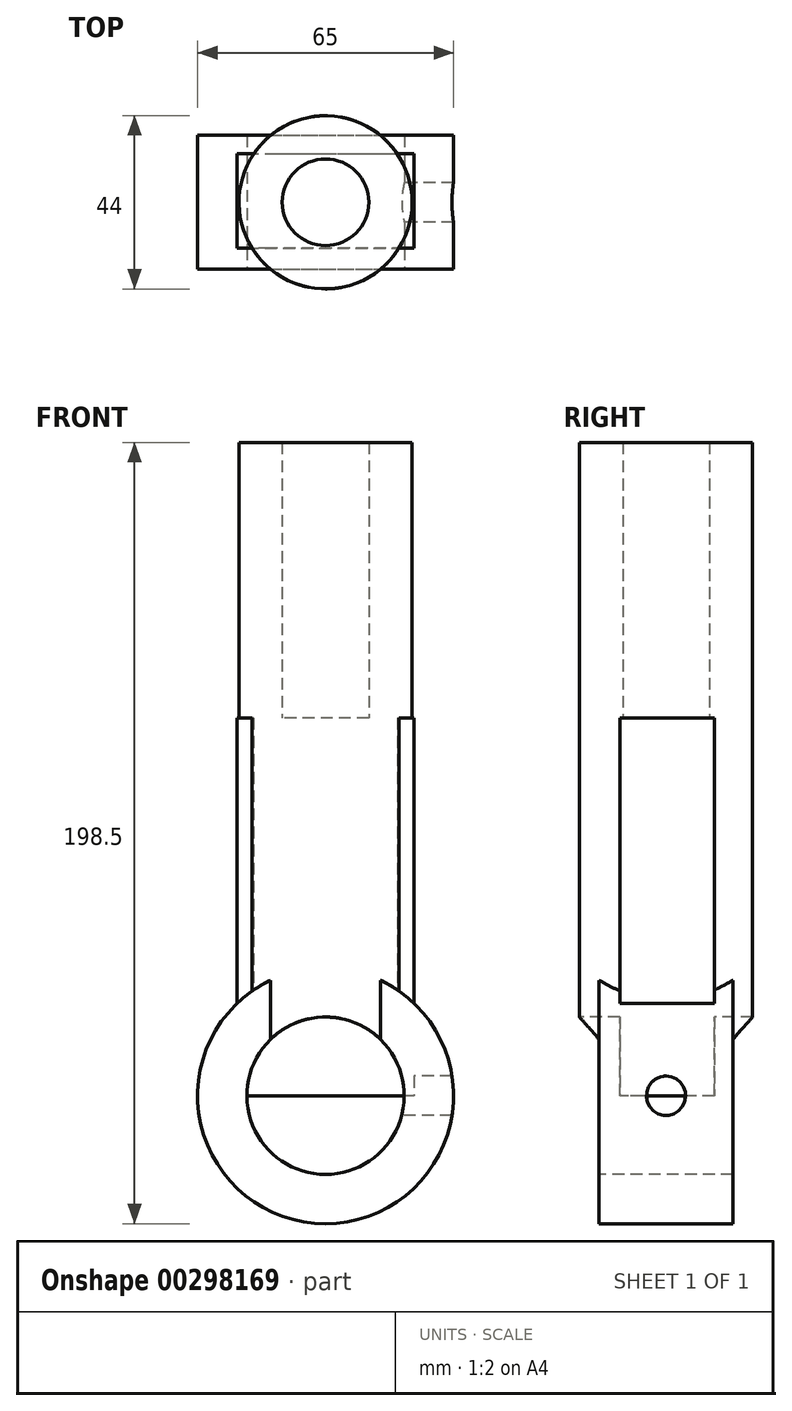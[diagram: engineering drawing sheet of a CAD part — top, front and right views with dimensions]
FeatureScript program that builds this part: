
annotation { "Feature Type Name" : "Feature", "Feature Type Description" : "" }
export const myFeature = defineFeature(function(context is Context, id is Id, definition is map)
    precondition{}
    {
        {
            var Q0;
            Q0=qCreatedBy(makeId("Front.planeOp"),FACE);
            var sketch = newSketch(context, id + "F0", { "sketchPlane" : qUnion([Q0])});
            skCircle(sketch, "E0", {"center": v(0, 0) * mm, "radius": 20 * mm});
            skCircle(sketch, "E1", {"center": v(0, 0) * mm, "radius": 32.5 * mm});
            skSolve(sketch);
        }
        {
            var Q0;
            Q0=makeQuery(id+"F0.imprint","IMPRINT",FACE,{"disambiguationData":[TD([[makeQuery(id+"F0.imprint","IMPRINT",EDGE,{"derivedFrom":sQuery(id+"F0.wireOp",EDGE,"E0")}),-1.0]])]});
            extrude(context, id + "F1", {"entities" : qUnion([Q0]), "endBound" : BoundingType.SYMMETRIC, "oppositeDirection" : true, "depth" : 34 * mm});
        }
        {
            var Q0;
            Q0=qCreatedBy(makeId("Front.planeOp"),FACE);
            var sketch = newSketch(context, id + "F2", { "sketchPlane" : qUnion([Q0])});
            skLineSegment(sketch, "E2", {"start": v(-22.5, 96) * mm, "end": v(22.5, 96) * mm});
            skLineSegment(sketch, "E3", {"start": v(0, 0) * mm, "end": v(0, 96) * mm, "construction": true});
            skLineSegment(sketch, "E4", {"start": v(-22.5, 96) * mm, "end": v(-22.5, 23.45) * mm});
            skLineSegment(sketch, "E5", {"start": v(22.5, 96) * mm, "end": v(22.5, 23.45) * mm});
            skSolve(sketch);
        }
        {
            var Q0;
            Q0=qCreatedBy(makeId("Top.planeOp"),FACE);
            var sketch = newSketch(context, id + "F3", { "sketchPlane" : qUnion([Q0])});
            skCircle(sketch, "E6", {"center": v(0, 0) * mm, "radius": 22 * mm});
            skCircle(sketch, "E7", {"center": v(0, 0) * mm, "radius": 11 * mm});
            skSolve(sketch);
        }
        {
            var Q0;
            Q0 = qSketchRegion(id + "F3", true);
            extrude(context, id + "F4", {"entities" : qUnion([Q0]), "operationType" : NewBodyOperationType.ADD, "depth" : 166 * mm});
        }
        {
            var Q0;
            Q0=qCreatedBy(makeId("Right.planeOp"),FACE);
            var sketch = newSketch(context, id + "F5", { "sketchPlane" : qUnion([Q0])});
            skCircle(sketch, "E8", {"center": v(0, 0) * mm, "radius": 5 * mm});
            skSolve(sketch);
        }
        {
            var Q0;
            Q0 = qSketchRegion(id + "F5", true);
            extrude(context, id + "F6", {"entities" : qUnion([Q0]), "operationType" : NewBodyOperationType.REMOVE, "endBound" : BoundingType.THROUGH_ALL, "depth" : 25 * mm});
        }
        {
            var Q0;
            Q0=qCreatedBy(makeId("Front.planeOp"),FACE);
            var sketch = newSketch(context, id + "F7", { "sketchPlane" : qUnion([Q0])});
            skCircle(sketch, "E9", {"center": v(0, 0) * mm, "radius": 20 * mm});
            skSolve(sketch);
        }
        {
            var Q0;
            Q0 = qSketchRegion(id + "F7", true);
            extrude(context, id + "F8", {"entities" : qUnion([Q0]), "operationType" : NewBodyOperationType.REMOVE, "endBound" : BoundingType.SYMMETRIC, "oppositeDirection" : true, "depth" : 50 * mm});
        }
        {
            var Q0;
            Q0=makeQuery(id+"F4.opExtrude","SWEPT_FACE",FACE,{"disambiguationData":[OSD([sQuery(id+"F3.wireOp",EDGE,"E6")])]});
            cPlane(context, id + "F9", {"entities" : qUnion([Q0]), "cplaneType" : CPlaneType.LINE_ANGLE, "offset" : 25 * mm, "angle" : 0 * degree, "width" : 150 * mm, "height" : 150 * mm});
        }
        {
            var Q0;
            Q0=qCreatedBy(id+"F9.planeOp",FACE);
            var sketch = newSketch(context, id + "F10", { "sketchPlane" : qUnion([Q0])});
            skLineSegment(sketch, "E10", {"start": v(0, 0) * mm, "end": v(-12.31, 0) * mm});
            skLineSegment(sketch, "E11", {"start": v(-12.31, 0) * mm, "end": v(-12.31, 96) * mm});
            skLineSegment(sketch, "E12", {"start": v(-12.31, 96) * mm, "end": v(11.69, 96) * mm});
            skLineSegment(sketch, "E13", {"start": v(11.69, 96) * mm, "end": v(11.69, 0) * mm});
            skLineSegment(sketch, "E14", {"start": v(11.69, 0) * mm, "end": v(0, 0) * mm});
            skSolve(sketch);
        }
        {
            var Q0;
            Q0 = qSketchRegion(id + "F10", true);
            extrude(context, id + "F11", {"entities" : qUnion([Q0]), "operationType" : NewBodyOperationType.ADD, "endBound" : BoundingType.SYMMETRIC, "depth" : 45 * mm});
        }
    });
